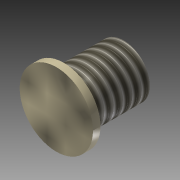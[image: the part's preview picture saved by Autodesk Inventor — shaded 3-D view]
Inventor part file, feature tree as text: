
AUTODESK INVENTOR PART (.ipt)
format: ipt  version: 2015 (Build 190159000, 159)  size: 97,280 bytes
history: native  units: in
note: dims shown in document units (in); Inventor stores cm internally (conversion verified against a paired STEP export)
features: extrude x2, sketch x2, thread x1
ambient origin geometry x8: Origin, YZ Plane, XZ Plane, XY Plane, X Axis, Y Axis, Z Axis, Center Point
bodies: Solid1 (feature_tree)
feature tree (5):
  extrude  "Extrusion1"  Depth=0.05in TaperAngle=0.0deg
  extrude  "Extrusion2"  Depth=0.4in TaperAngle=0.0deg
  thread  "Thread1"  [1 undecoded]
  sketch  "Sketch1"  dims[d0=0.49in d1=0.05in d2=0.0in]
  sketch  "Sketch2"  dims[d3=0.35in d4=0.4in d5=0.0in d6=1.0in d7=0.0in]
note: 1 required parameter value undecoded (feature->parameter linkage not recoverable at this tier; creation-order binding heuristic only, values carry confidence <= 0.55)
